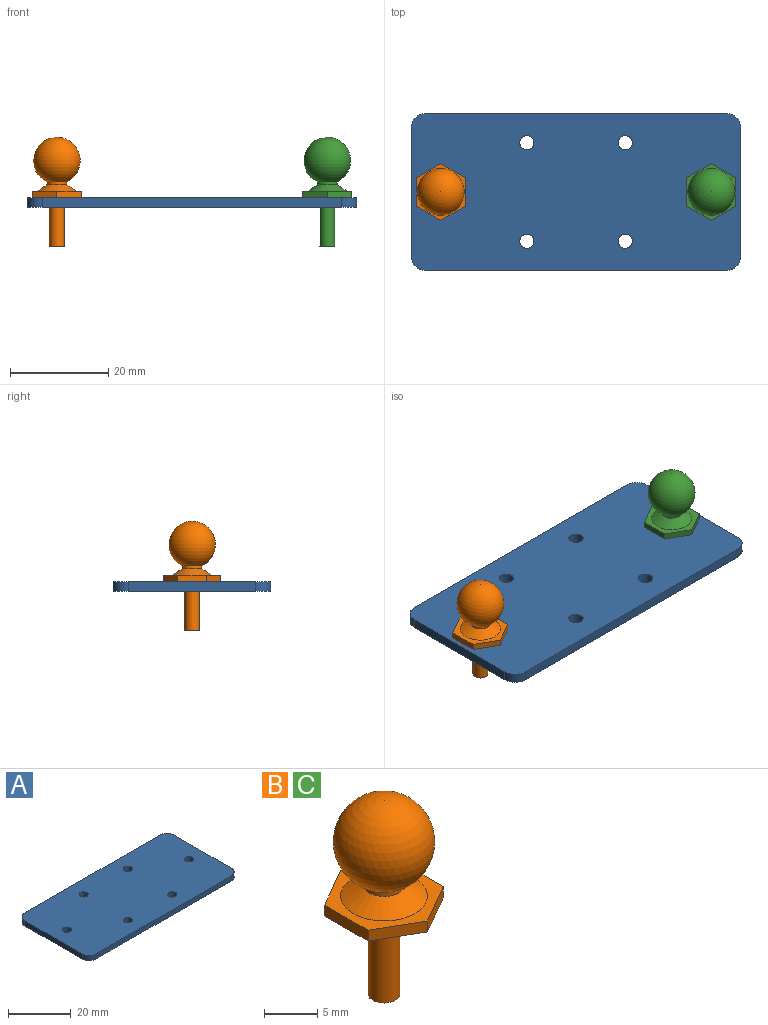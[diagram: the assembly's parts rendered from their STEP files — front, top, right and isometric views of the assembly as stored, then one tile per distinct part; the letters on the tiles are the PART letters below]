
ASSEMBLY  parts=3 mates=2
PART A: 16 faces, bbox 67x32x2 mm
  f0: plane 26x2mm, normal (1,0,0), area 52mm2, adj f1,f13,f14,f15
  f1: cylinder r=3mm len=3mm, axis (0,0,-1), area 9.4mm2, adj f0,f2,f14,f15
  f2: plane 61x2mm, normal (0,1,0), area 122mm2, adj f1,f3,f14,f15
  f3: cylinder r=3mm len=3mm, axis (0,0,-1), area 9.4mm2, adj f2,f4,f14,f15
  f4: plane 26x2mm, normal (-1,0,0), area 52mm2, adj f3,f5,f14,f15
  f5: cylinder r=3mm len=3mm, axis (0,0,-1), area 9.4mm2, adj f4,f6,f14,f15
  f6: plane 61x2mm, normal (0,-1,0), area 122mm2, adj f5,f13,f14,f15
  f7: cylinder r=1.45mm len=2.9mm, axis (0,0,-1), area 18.2mm2, adj f14,f15
  f8: cylinder r=1.45mm len=2.9mm, axis (0,0,-1), area 18.2mm2, adj f14,f15
  f9: cylinder r=1.45mm len=2.9mm, axis (0,0,-1), area 18.2mm2, adj f14,f15
  f10: cylinder r=1.45mm len=2.9mm, axis (0,0,-1), area 18.2mm2, adj f14,f15
  f11: cylinder r=1.45mm len=2.9mm, axis (0,0,-1), area 18.2mm2, adj f14,f15
  f12: cylinder r=1.45mm len=2.9mm, axis (0,0,-1), area 18.2mm2, adj f14,f15
  f13: cylinder r=3mm len=3mm, axis (0,0,-1), area 9.4mm2, adj f0,f6,f14,f15
  f14: plane 67x32mm, normal (0,0,1), area 2096.6mm2, adj f0,f1,f2,f3,f4,f5,f6,f7
  f15: plane 67x32mm, normal (0,0,-1), area 2096.6mm2, adj f0,f1,f2,f3,f4,f5,f6,f7
PART B: 13 faces, bbox 10x11.5x22.3 mm
  f0: plane 11.55x10mm, normal (0,0,1), area 34.4mm2, adj f3,f4,f5,f6,f7,f8,f9
  f1: cylinder r=2mm len=4mm, axis (0,0,1), area 7.1mm2, adj f2,f3
  f2: sphere r=4.76mm, area 271.8mm2, adj f1
  f3: cone r=2mm half-angle=57deg, axis (0,0,-1), area 47.2mm2, adj f0,f1
  f4: plane 5.77x1.25mm, normal (1,0,0), area 7.2mm2, adj f0,f5,f9,f12
  f5: plane 5x2.89mm, normal (0.5,0.87,0), area 7.2mm2, adj f0,f4,f6,f12
  f6: plane 5x2.89mm, normal (-0.5,0.87,0), area 7.2mm2, adj f0,f5,f7,f12
  f7: plane 5.77x1.25mm, normal (-1,0,0), area 7.2mm2, adj f0,f6,f8,f12
  f8: plane 5x2.89mm, normal (-0.5,-0.87,0), area 7.2mm2, adj f0,f7,f9,f12
  f9: plane 5x2.89mm, normal (0.5,-0.87,0), area 7.2mm2, adj f0,f4,f8,f12
  f10: plane 3x3mm, normal (0,0,-1), area 7.1mm2, adj f11
  f11: cylinder r=1.5mm len=10mm, axis (0,0,1), area 94.2mm2, adj f10,f12
  f12: plane 11.55x10mm, normal (0,0,-1), area 79.5mm2, adj f4,f5,f6,f7,f8,f9,f11
PART C: same geometry as B
PLACE A at identity fixed
PLACE B t=(-27.5,0,2)mm
PLACE C t=(27.5,0,2)mm
MATE fastened B.f3 <-> A.f10  axis (0,0,-1) through (-27.5,0,2)mm
MATE fastened C.f3 <-> A.f11  axis (0,0,-1) through (27.5,0,2)mm
